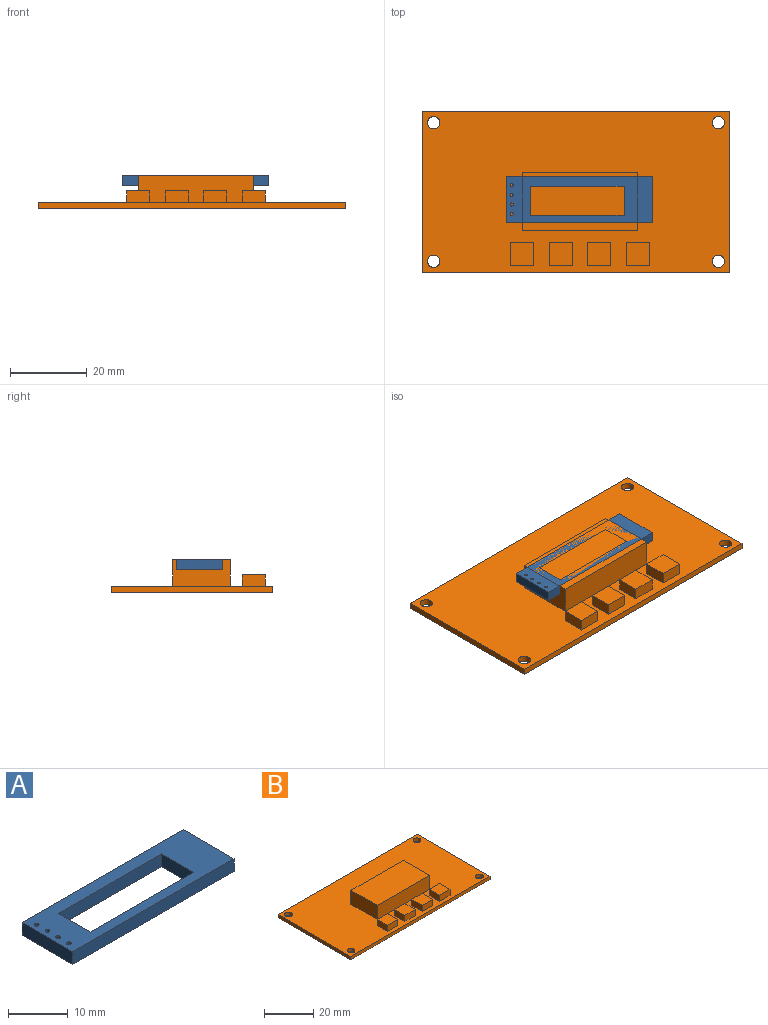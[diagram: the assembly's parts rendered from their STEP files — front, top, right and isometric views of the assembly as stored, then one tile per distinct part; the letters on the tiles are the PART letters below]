
ASSEMBLY  parts=2 mates=1
PART A: 14 faces, bbox 38x12x2.6 mm
  f0: plane 38x2.6mm, normal (0,1,0), area 98.8mm2, adj f1,f11,f12,f13
  f1: plane 12x2.6mm, normal (-1,0,0), area 31.2mm2, adj f0,f2,f12,f13
  f2: plane 38x2.6mm, normal (0,-1,0), area 98.8mm2, adj f1,f11,f12,f13
  f3: plane 7.58x2.6mm, normal (1,0,0), area 19.7mm2, adj f4,f6,f12,f13
  f4: plane 24.38x2.6mm, normal (0,-1,0), area 63.4mm2, adj f3,f5,f12,f13
  f5: plane 7.58x2.6mm, normal (-1,0,0), area 19.7mm2, adj f4,f6,f12,f13
  f6: plane 24.38x2.6mm, normal (0,1,0), area 63.4mm2, adj f3,f5,f12,f13
  f7: cylinder r=0.4mm len=2.6mm, axis (0,0,-1), area 6.5mm2, adj f12,f13
  f8: cylinder r=0.4mm len=2.6mm, axis (0,0,-1), area 6.5mm2, adj f12,f13
  f9: cylinder r=0.4mm len=2.6mm, axis (0,0,-1), area 6.5mm2, adj f12,f13
  f10: cylinder r=0.4mm len=2.6mm, axis (0,0,-1), area 6.5mm2, adj f12,f13
  f11: plane 12x2.6mm, normal (1,0,0), area 31.2mm2, adj f0,f2,f12,f13
  f12: plane 38x12mm, normal (0,0,1), area 269.2mm2, adj f0,f1,f2,f3,f4,f5,f6,f7
  f13: plane 38x12mm, normal (0,0,-1), area 269.2mm2, adj f0,f1,f2,f3,f4,f5,f6,f7
PART B: 35 faces, bbox 80x42x8.6 mm
  f0: plane 80x42mm, normal (0,0,1), area 2733.8mm2, adj f1,f2,f3,f4,f5,f6,f7,f8
  f1: plane 80x1.6mm, normal (0,1,0), area 128mm2, adj f0,f2,f8,f9
  f2: plane 42x1.6mm, normal (-1,0,0), area 67.2mm2, adj f0,f1,f3,f9
  f3: plane 80x1.6mm, normal (0,-1,0), area 128mm2, adj f0,f2,f8,f9
  f4: cylinder r=1.6mm len=3.2mm, axis (0,0,-1), area 16.1mm2, adj f0,f9
  f5: cylinder r=1.6mm len=3.2mm, axis (0,0,-1), area 16.1mm2, adj f0,f9
  f6: cylinder r=1.6mm len=3.2mm, axis (0,0,-1), area 16.1mm2, adj f0,f9
  f7: cylinder r=1.6mm len=3.2mm, axis (0,0,-1), area 16.1mm2, adj f0,f9
  f8: plane 42x1.6mm, normal (1,0,0), area 67.2mm2, adj f0,f1,f3,f9
  f9: plane 80x42mm, normal (0,0,-1), area 3327.8mm2, adj f1,f2,f3,f4,f5,f6,f7,f8
  f10: plane 30x7mm, normal (0,1,0), area 210mm2, adj f0,f11,f13,f14
  f11: plane 15x7mm, normal (-1,0,0), area 105mm2, adj f0,f10,f12,f14
  f12: plane 30x7mm, normal (0,-1,0), area 210mm2, adj f0,f11,f13,f14
  f13: plane 15x7mm, normal (1,0,0), area 105mm2, adj f0,f10,f12,f14
  f14: plane 30x15mm, normal (0,0,1), area 450mm2, adj f10,f11,f12,f13
  f15: plane 6x3mm, normal (0,1,0), area 18mm2, adj f0,f16,f18,f19
  f16: plane 6x3mm, normal (-1,0,0), area 18mm2, adj f0,f15,f17,f19
  f17: plane 6x3mm, normal (0,-1,0), area 18mm2, adj f0,f16,f18,f19
  f18: plane 6x3mm, normal (1,0,0), area 18mm2, adj f0,f15,f17,f19
  f19: plane 6x6mm, normal (0,0,1), area 36mm2, adj f15,f16,f17,f18
  f20: plane 6x3mm, normal (1,0,0), area 18mm2, adj f0,f21,f23,f24
  f21: plane 6x3mm, normal (0,1,0), area 18mm2, adj f0,f20,f22,f24
  f22: plane 6x3mm, normal (-1,0,0), area 18mm2, adj f0,f21,f23,f24
  f23: plane 6x3mm, normal (0,-1,0), area 18mm2, adj f0,f20,f22,f24
  f24: plane 6x6mm, normal (0,0,1), area 36mm2, adj f20,f21,f22,f23
  f25: plane 6x3mm, normal (1,0,0), area 18mm2, adj f0,f26,f28,f29
  f26: plane 6x3mm, normal (0,1,0), area 18mm2, adj f0,f25,f27,f29
  f27: plane 6x3mm, normal (-1,0,0), area 18mm2, adj f0,f26,f28,f29
  f28: plane 6x3mm, normal (0,-1,0), area 18mm2, adj f0,f25,f27,f29
  f29: plane 6x6mm, normal (0,0,1), area 36mm2, adj f25,f26,f27,f28
  f30: plane 6x3mm, normal (1,0,0), area 18mm2, adj f0,f31,f33,f34
  f31: plane 6x3mm, normal (0,1,0), area 18mm2, adj f0,f30,f32,f34
  f32: plane 6x3mm, normal (-1,0,0), area 18mm2, adj f0,f31,f33,f34
  f33: plane 6x3mm, normal (0,-1,0), area 18mm2, adj f0,f30,f32,f34
  f34: plane 6x6mm, normal (0,0,1), area 36mm2, adj f30,f31,f32,f33
PLACE A t=(-3.44,-0.98,7.07)mm
PLACE B t=(-6.08,-2.83,1.07)mm fixed
MATE fastened B.f14 <-> A.f12  axis (0,0,1) through (-3.44,-8.98,9.67)mm
